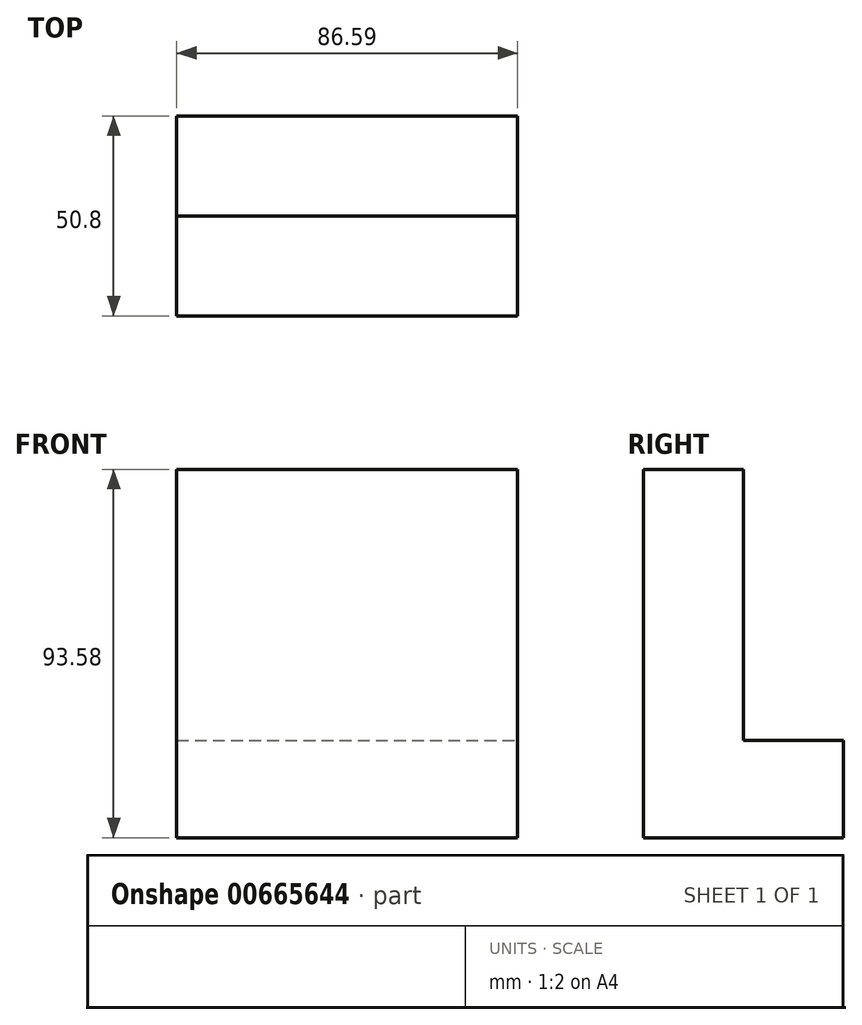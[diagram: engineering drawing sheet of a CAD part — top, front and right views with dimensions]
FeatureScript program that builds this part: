
annotation { "Feature Type Name" : "Feature", "Feature Type Description" : "" }
export const myFeature = defineFeature(function(context is Context, id is Id, definition is map)
    precondition{}
    {
        {
            var Q0;
            Q0=qCreatedBy(makeId("Front.planeOp"),FACE);
            var sketch = newSketch(context, id + "F0", { "sketchPlane" : qUnion([Q0])});
            skLineSegment(sketch, "E0", {"start": v(-43.7, -24.37) * mm, "end": v(-43.7, 48.03) * mm});
            skLineSegment(sketch, "E1", {"start": v(-43.7, 48.03) * mm, "end": v(-43.7, 56.25) * mm});
            skLineSegment(sketch, "E2", {"start": v(-43.7, 56.25) * mm, "end": v(42.88, 56.25) * mm});
            skLineSegment(sketch, "E3", {"start": v(42.88, 56.25) * mm, "end": v(42.88, -26.43) * mm});
            skLineSegment(sketch, "E4", {"start": v(42.88, -26.43) * mm, "end": v(42.88, -37.33) * mm});
            skLineSegment(sketch, "E5", {"start": v(42.88, -37.33) * mm, "end": v(-43.7, -37.33) * mm});
            skLineSegment(sketch, "E6", {"start": v(-43.7, -37.33) * mm, "end": v(-43.7, -24.37) * mm});
            skLineSegment(sketch, "E7", {"start": v(-43.7, -24.37) * mm, "end": v(-43.7, -37.33) * mm});
            skSolve(sketch);
        }
        {
            var Q0;
            Q0 = qSketchRegion(id + "F0", true);
            extrude(context, id + "F1", {"entities" : qUnion([Q0]), "depth" : 25.4 * mm, "offsetDistance" : 25.4 * mm});
        }
        {
            var Q0;
            Q0=makeQuery(id+"F1.opExtrude","CAP_FACE",FACE,{"disambiguationData":[OSD([sQuery(id+"F0.wireOp",EDGE,"E0"),sQuery(id+"F0.wireOp",EDGE,"E1"),sQuery(id+"F0.wireOp",EDGE,"E2"),sQuery(id+"F0.wireOp",EDGE,"E3"),sQuery(id+"F0.wireOp",EDGE,"E4"),sQuery(id+"F0.wireOp",EDGE,"E5"),sQuery(id+"F0.wireOp",EDGE,"E7")])],"isStart":true});
            var sketch = newSketch(context, id + "F2", { "sketchPlane" : qUnion([Q0])});
            skLineSegment(sketch, "E8.top", {"start": v(-42.88, -37.33) * mm, "end": v(43.7, -37.33) * mm});
            skLineSegment(sketch, "E8.left", {"start": v(-42.88, 0) * mm, "end": v(-42.88, -37.33) * mm});
            skLineSegment(sketch, "E8.right", {"start": v(43.7, 0) * mm, "end": v(43.7, -37.33) * mm});
            skLineSegment(sketch, "E9", {"start": v(43.7, -12.62) * mm, "end": v(-42.88, -12.62) * mm});
            skLineSegment(sketch, "E10", {"start": v(43.7, -12.62) * mm, "end": v(43.7, -37.33) * mm});
            skLineSegment(sketch, "E11", {"start": v(43.7, -37.33) * mm, "end": v(43.7, -12.62) * mm});
            skLineSegment(sketch, "E12", {"start": v(43.7, -37.33) * mm, "end": v(-42.88, -37.33) * mm});
            skLineSegment(sketch, "E13", {"start": v(-42.88, -37.33) * mm, "end": v(-42.88, -12.62) * mm});
            skLineSegment(sketch, "E14", {"start": v(-42.88, -12.62) * mm, "end": v(-42.88, -37.33) * mm});
            skSolve(sketch);
        }
        {
            var Q0;
            Q0 = qSketchRegion(id + "F2", true);
            extrude(context, id + "F3", {"entities" : qUnion([Q0]), "operationType" : NewBodyOperationType.ADD, "depth" : 25.4 * mm, "offsetDistance" : 25.4 * mm});
        }
    });
